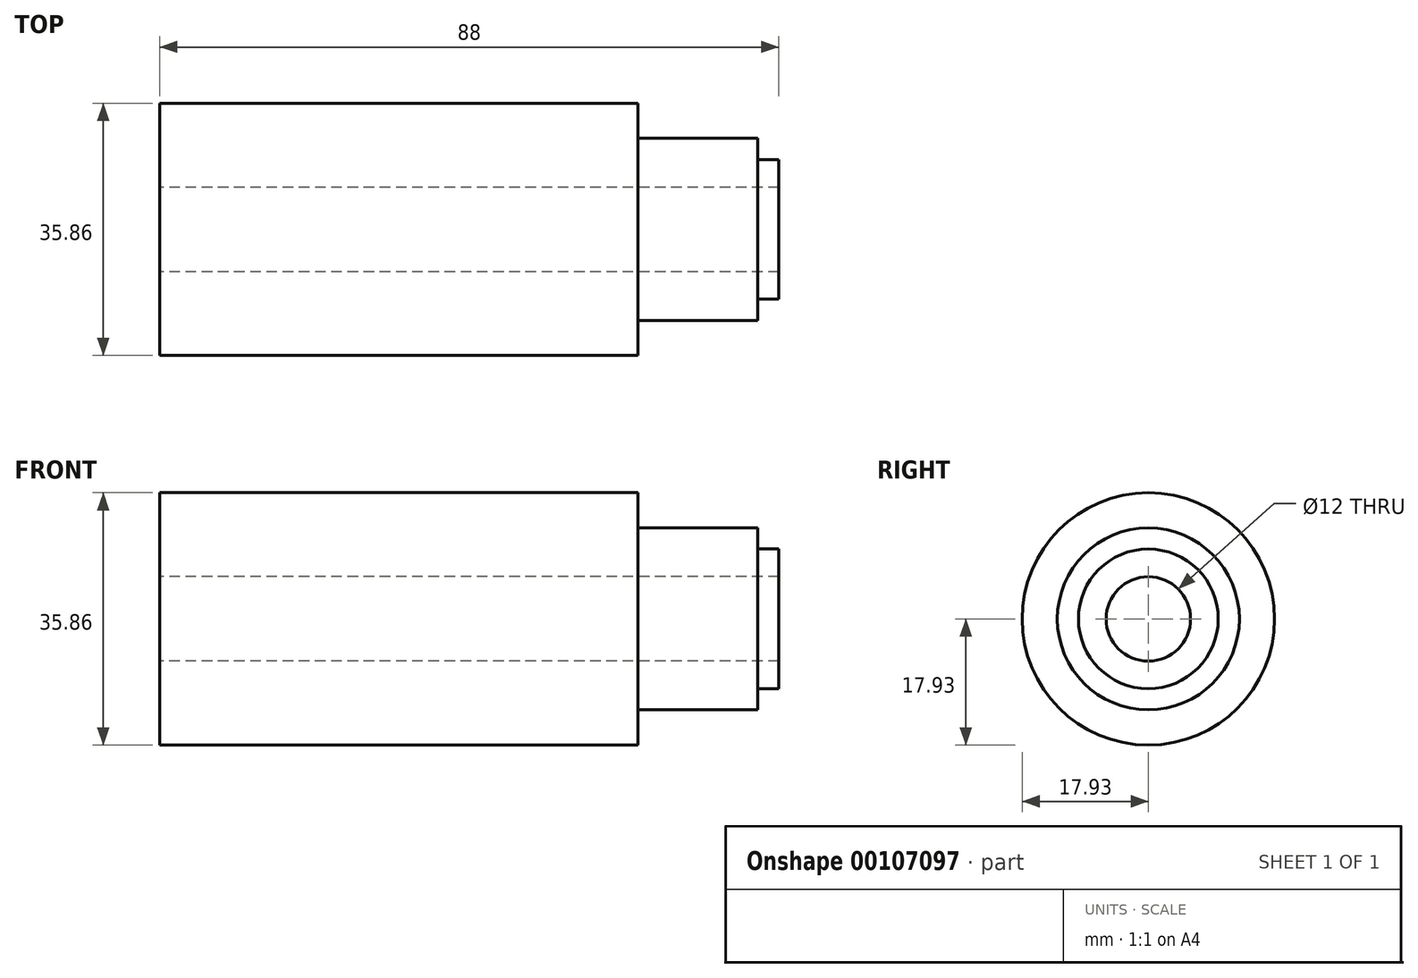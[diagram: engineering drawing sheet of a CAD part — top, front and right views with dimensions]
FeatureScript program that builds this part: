
annotation { "Feature Type Name" : "Feature", "Feature Type Description" : "" }
export const myFeature = defineFeature(function(context is Context, id is Id, definition is map)
    precondition{}
    {
        {
            var Q0;
            Q0=qCreatedBy(makeId("Top.planeOp"),FACE);
            var sketch = newSketch(context, id + "F0", { "sketchPlane" : qUnion([Q0])});
            skLineSegment(sketch, "E0", {"start": v(0, 0) * mm, "end": v(0, 17.93) * mm});
            skLineSegment(sketch, "E1", {"start": v(0, 17.93) * mm, "end": v(68, 17.93) * mm});
            skLineSegment(sketch, "E2", {"start": v(68, 17.93) * mm, "end": v(68, 12.93) * mm});
            skLineSegment(sketch, "E3", {"start": v(68, 12.93) * mm, "end": v(85, 12.93) * mm});
            skLineSegment(sketch, "E4", {"start": v(85, 12.93) * mm, "end": v(85, 9.93) * mm});
            skLineSegment(sketch, "E5", {"start": v(85, 9.93) * mm, "end": v(88, 9.93) * mm});
            skLineSegment(sketch, "E6", {"start": v(88, 9.93) * mm, "end": v(88, 0) * mm});
            skLineSegment(sketch, "E7", {"start": v(1.5, 17.93) * mm, "end": v(1.5, 0) * mm, "construction": true});
            skLineSegment(sketch, "E8", {"start": v(1.5, 8.96) * mm, "end": v(12, 8.96) * mm, "construction": true});
            skLineSegment(sketch, "E9", {"start": v(12, 8.96) * mm, "end": v(12, 0) * mm, "construction": true});
            skLineSegment(sketch, "E10", {"start": v(12, 4.48) * mm, "end": v(15, 4.48) * mm, "construction": true});
            skLineSegment(sketch, "E11", {"start": v(15, 4.48) * mm, "end": v(15, 11.97) * mm, "construction": true});
            skLineSegment(sketch, "E12", {"start": v(15, 11.97) * mm, "end": v(22, 11.97) * mm, "construction": true});
            skLineSegment(sketch, "E13", {"start": v(22, 11.97) * mm, "end": v(22, 0) * mm, "construction": true});
            skLineSegment(sketch, "E14", {"start": v(22, 7.82) * mm, "end": v(30, 7.82) * mm, "construction": true});
            skLineSegment(sketch, "E15", {"start": v(30, 7.82) * mm, "end": v(30, 0) * mm, "construction": true});
            skLineSegment(sketch, "E16", {"start": v(30, 0) * mm, "end": v(88, 0) * mm, "construction": true});
            skLineSegment(sketch, "E17", {"start": v(0, 0) * mm, "end": v(88, 0) * mm});
            skSolve(sketch);
        }
        {
            var Q0;
            Q0=makeQuery(id+"F0.imprint","IMPRINT",FACE,{"disambiguationData":[TD([[makeQuery(id+"F0.imprint","IMPRINT",EDGE,{"derivedFrom":sQuery(id+"F0.wireOp",EDGE,"E0")}),-1.0]])]});
            var Q1;
            Q1=sQuery(id+"F0.wireOp",EDGE,"E17");
            revolve(context, id + "F1", {"entities" : qUnion([Q0]), "axis" : qUnion([Q1]), "revolveType" : RevolveType.FULL});
        }
        {
            var Q0;
            Q0=qCreatedBy(makeId("Right.planeOp"),FACE);
            var sketch = newSketch(context, id + "F2", { "sketchPlane" : qUnion([Q0])});
            skCircle(sketch, "E18", {"center": v(0, 0) * mm, "radius": 6 * mm});
            skSolve(sketch);
        }
        {
            var Q0;
            Q0 = qSketchRegion(id + "F2", true);
            extrude(context, id + "F3", {"entities" : qUnion([Q0]), "operationType" : NewBodyOperationType.REMOVE, "endBound" : BoundingType.THROUGH_ALL, "depth" : 25.4 * mm});
        }
    });
